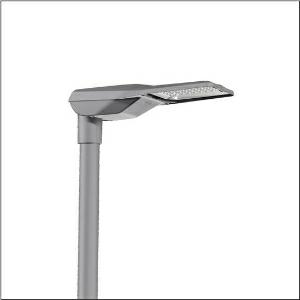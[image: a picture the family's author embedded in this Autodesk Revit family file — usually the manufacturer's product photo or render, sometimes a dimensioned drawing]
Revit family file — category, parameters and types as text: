
# Revit family: streetlight_sl_21_iq_mini___st0_5a_5xe2b31g08hb_4c73
name_source: partatom
category: Lighting Fixtures
units: mm (PartAtom-declared; Revit-internal decimal feet)

## family parameters
Cut with Voids When Loaded = No
Host = Face
Light Source = No
Part Type = Normal
Room Calculation Point = No
Round Connector Dimension = Use Diameter
Shared = No

## types (1)
- --- (1 x LED, 9450 lm, 70.9 W, 3000K)
    Apparent Load = 71 VA
    CIE Flux Codes = 41 75 97 100 100
    Color Rendering = 70
    Color Temperature = 3000K
    Default Elevation = 1800 mm
    Description = Streetlight SL 21 iQ mini, mast luminaire, primary light control with lens, of PMMA, primary optical cover: cover, of toughened safety glass, transparent, light distribution: ST0.5a, light emission: direct distribution, primary light characteristic: asymmetric, installation type: post-top, side-entry, LED, High Power LED, rated luminous flux: 9.450lm, luminous efficacy: 133lm/W, light colour: 730, colour temperature: 3000K, control gear: iQ Street-Remote, control: Street-Remote, Auto-Match, Temp-Guard, Lumen-Switch, Night-Set, Smart-Wire, Light-Fading, Desk-Remote (wireless, voltage-free reading and setting of iQ features in the workshop via application-optimized NFC function/RFID function), optimised constant luminous flux control (CLO 2.0), pre-setting: linear dimming characteristic, mains connection: 220..240V, AC, 50/60Hz, start of lifetime: 71W, end of service life: 75W, reduction: 31W, luminaire housing, of diecast aluminium, powder-coated, Siteco® metallic grey (DB 702S), corrosivity category C5 mid according to DIN EN ISO 12944, please order mast flange separately, inclination adjustable: 0°, 5°, 10°, 15°, sealing non-destructively replaceable, multi-level sealing system, length: 628mm, width: 235mm, height: 110mm, mast flange for spigot size: 42mm (side-entry): 5XC10008XM4, 60/48mm (side-entry/post-top): 5XC10108XM2, 76/60mm (side-entry/post-top): 5XC10108XM1, mounting height: 4..8m, protection rating (complete): IP66, insulation class (complete): insulation class II (safety insulation), certification: CE, ENEC, ENEC+, VDE, impact resistance: IK10, permissible operating ambient temperature for outdoor applications: -40..+50°C, standard-compliant lighting for roads and squares, packaging unit: 1 piece

Light Distribution: ST0.5a
    Height = 110 mm
    Lamp = 1 x LED
    Lamp Light Flux = 9450 lm
    Lamp Power = 70.9 W
    Lamp count = 1
    Length = 625 mm
    Luminous efficacy = 133 lm/W
    Manufacturer = Siteco
    ModVariant = No
    Model = 5XE2B31G08HB
    Number of Poles = 1
    OnlyDefault = Yes
    Power Factor = 1
    Product Name = Streetlight SL 21 iQ mini | ST0.5a
    Product group = mast luminaire | pylon top
    ProductGroupID = 6100
    Protection Class = Protection class II
    Protection Degree = IP 66
    RLX_Detail_Level = 1
    RLX_Emergency_Light_Flux = 0 lm
    RLX_Emergency_Type = 0
    RLX_Emergency_Type_DB = No
    RlxData = <blob elided: 37277 chars, md5=4383a885>
    Socket = socket
    Standby Power = 0 W
    System Light Flux = 9450 lm
    System Power = 71 W
    Type Comments = factory setting: luminous flux: 100 % | dim-lin: 254 | 711 mA
    Type Image = l_1003519.jpg
    URL = http://relux.com
    VarID = @adj_158606
    Voltage = 0 V
    Weight = 0.00 kg
    Width = 234 mm

## geometry (parser evidence)
native form markers: Blend x4, Sweep x13
no freeform markers — native parametric forms only
